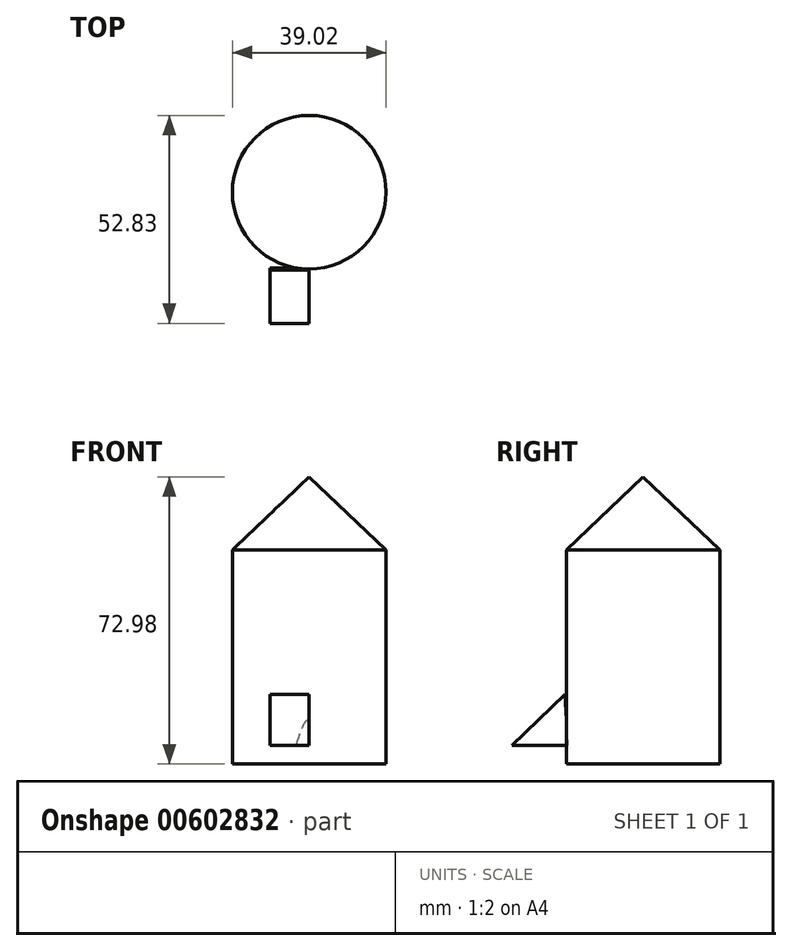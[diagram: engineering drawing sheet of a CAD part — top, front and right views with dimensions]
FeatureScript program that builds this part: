
annotation { "Feature Type Name" : "Feature", "Feature Type Description" : "" }
export const myFeature = defineFeature(function(context is Context, id is Id, definition is map)
    precondition{}
    {
        {
            var Q0;
            Q0=qCreatedBy(makeId("Front.planeOp"),FACE);
            var sketch = newSketch(context, id + "F0", { "sketchPlane" : qUnion([Q0])});
            skLineSegment(sketch, "E0", {"start": v(0, 41.63) * mm, "end": v(19.51, 23.03) * mm});
            skLineSegment(sketch, "E1", {"start": v(19.51, 23.03) * mm, "end": v(19.51, -31.35) * mm});
            skLineSegment(sketch, "E2", {"start": v(19.51, -31.35) * mm, "end": v(0, -31.35) * mm});
            skLineSegment(sketch, "E3", {"start": v(0, 41.63) * mm, "end": v(0, -31.35) * mm});
            skSolve(sketch);
        }
        {
            var Q0;
            Q0=makeQuery(id+"F0.imprint","IMPRINT",FACE,{"disambiguationData":[TD([[makeQuery(id+"F0.imprint","IMPRINT",EDGE,{"derivedFrom":sQuery(id+"F0.wireOp",EDGE,"E0")}),-1.0]])]});
            var Q1;
            Q1=sQuery(id+"F0.wireOp",EDGE,"E3");
            revolve(context, id + "F1", {"entities" : qUnion([Q0]), "axis" : qUnion([Q1]), "revolveType" : RevolveType.FULL});
        }
        {
            var Q0;
            Q0=qCreatedBy(makeId("Right.planeOp"),FACE);
            var sketch = newSketch(context, id + "F2", { "sketchPlane" : qUnion([Q0])});
            skLineSegment(sketch, "E4", {"start": v(-19.8, -13.6) * mm, "end": v(-33.32, -26.56) * mm});
            skLineSegment(sketch, "E5", {"start": v(-19.23, -26.56) * mm, "end": v(-33.32, -26.56) * mm});
            skLineSegment(sketch, "E6", {"start": v(-19.8, -13.6) * mm, "end": v(-19.23, -26.56) * mm});
            skSolve(sketch);
        }
        {
            var Q0;
            Q0=makeQuery(id+"F2.imprint","IMPRINT",FACE,{"disambiguationData":[TD([[makeQuery(id+"F2.imprint","IMPRINT",EDGE,{"derivedFrom":sQuery(id+"F2.wireOp",EDGE,"E4")}),1.0]])]});
            extrude(context, id + "F3", {"entities" : qUnion([Q0]), "operationType" : NewBodyOperationType.ADD, "oppositeDirection" : true, "depth" : 10 * mm, "offsetDistance" : 25 * mm});
        }
    });
